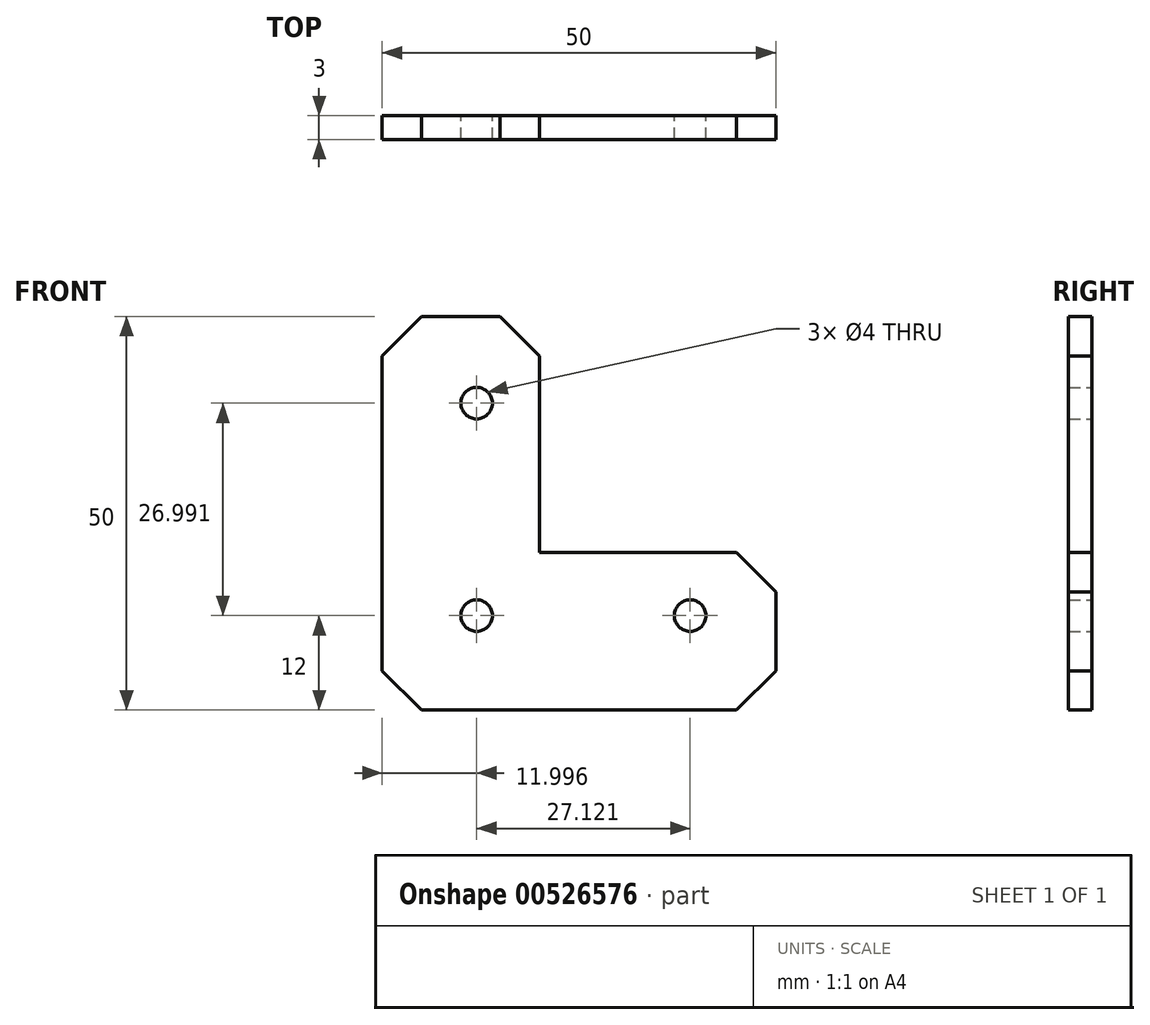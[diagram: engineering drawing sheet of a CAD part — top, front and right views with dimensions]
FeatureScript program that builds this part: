
annotation { "Feature Type Name" : "Feature", "Feature Type Description" : "" }
export const myFeature = defineFeature(function(context is Context, id is Id, definition is map)
    precondition{}
    {
        {
            var Q0;
            Q0=qCreatedBy(makeId("Front.planeOp"),FACE);
            var sketch = newSketch(context, id + "F0", { "sketchPlane" : qUnion([Q0])});
            skLineSegment(sketch, "E0", {"start": v(-55.77, 50) * mm, "end": v(-55.77, 0) * mm});
            skLineSegment(sketch, "E1", {"start": v(-55.77, 0) * mm, "end": v(-5.77, 0) * mm});
            skLineSegment(sketch, "E2", {"start": v(-5.77, 0) * mm, "end": v(-5.77, 20) * mm});
            skLineSegment(sketch, "E3", {"start": v(-5.77, 20) * mm, "end": v(-35.77, 20) * mm});
            skLineSegment(sketch, "E4", {"start": v(-35.77, 20) * mm, "end": v(-35.77, 50) * mm});
            skLineSegment(sketch, "E5", {"start": v(-35.77, 50) * mm, "end": v(-55.77, 50) * mm});
            skCircle(sketch, "E6", {"center": v(-43.77, 39) * mm, "radius": 2 * mm});
            skPoint(sketch, "E6.centerSnap0", {"position": v(-45.77, 50) * mm});
            skCircle(sketch, "E7", {"center": v(-16.65, 12) * mm, "radius": 2 * mm});
            skPoint(sketch, "E7.centerSnap0", {"position": v(-5.77, 10) * mm});
            skCircle(sketch, "E8", {"center": v(-43.77, 12) * mm, "radius": 2 * mm});
            skSolve(sketch);
        }
        {
            var Q0;
            Q0=qSketchRegion(id+"F0",true);
            extrude(context, id + "F1", {"entities" : qUnion([Q0]), "depth" : 3 * mm, "offsetDistance" : 25 * mm});
        }
        {
            var Q0;
            Q0=makeQuery(id+"F1.opExtrude","SWEPT_EDGE",EDGE,{"disambiguationData":[OSD([sQuery(id+"F0.wireOp",EDGE,"E0"),sQuery(id+"F0.wireOp",EDGE,"E5")])]});
            var Q1;
            Q1=makeQuery(id+"F1.opExtrude","SWEPT_EDGE",EDGE,{"disambiguationData":[OSD([sQuery(id+"F0.wireOp",EDGE,"E4"),sQuery(id+"F0.wireOp",EDGE,"E5")])]});
            var Q2;
            Q2=makeQuery(id+"F1.opExtrude","SWEPT_EDGE",EDGE,{"disambiguationData":[OSD([sQuery(id+"F0.wireOp",EDGE,"E2"),sQuery(id+"F0.wireOp",EDGE,"E3")])]});
            var Q3;
            Q3=makeQuery(id+"F1.opExtrude","SWEPT_EDGE",EDGE,{"disambiguationData":[OSD([sQuery(id+"F0.wireOp",EDGE,"E1"),sQuery(id+"F0.wireOp",EDGE,"E2")])]});
            var Q4;
            Q4=makeQuery(id+"F1.opExtrude","SWEPT_EDGE",EDGE,{"disambiguationData":[OSD([sQuery(id+"F0.wireOp",EDGE,"E0"),sQuery(id+"F0.wireOp",EDGE,"E1")])]});
            chamfer(context, id + "F2", {"entities" : qUnion([Q0, Q1, Q2, Q3, Q4]), "width" : 5 * mm, "tangentPropagation" : true});
        }
    });
